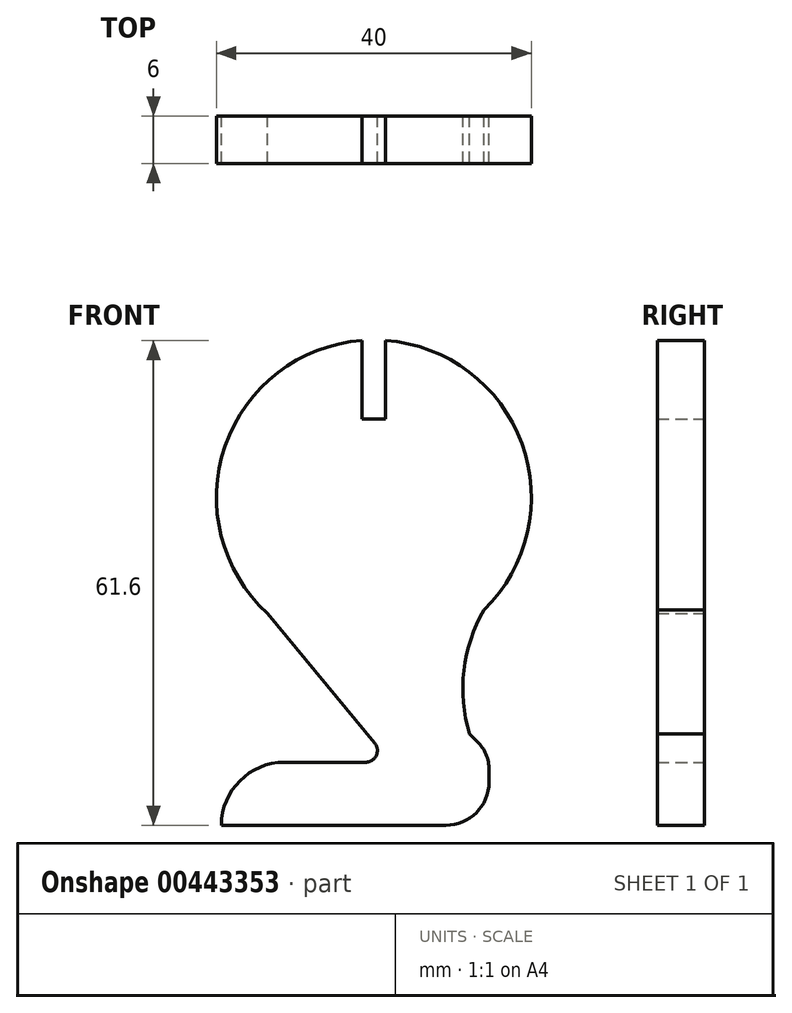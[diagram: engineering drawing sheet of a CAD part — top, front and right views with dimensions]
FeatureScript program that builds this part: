
annotation { "Feature Type Name" : "Feature", "Feature Type Description" : "" }
export const myFeature = defineFeature(function(context is Context, id is Id, definition is map)
    precondition{}
    {
        {
            var Q0;
            Q0=qCreatedBy(makeId("Front.planeOp"),FACE);
            var sketch = newSketch(context, id + "F0", { "sketchPlane" : qUnion([Q0])});
            skArc(sketch, "E0", {"start": v(-1.5, 36.94) * mm, "mid": v(-18.9, 23.55) * mm, "end": v(-13.52, 2.26) * mm});
            skLineSegment(sketch, "E1", {"start": v(-1.5, 36.94) * mm, "end": v(-1.5, 26.94) * mm});
            skLineSegment(sketch, "E2", {"start": v(-1.5, 26.94) * mm, "end": v(1.5, 26.94) * mm});
            skLineSegment(sketch, "E3", {"start": v(1.5, 26.94) * mm, "end": v(1.5, 36.94) * mm});
            skLineSegment(sketch, "E4", {"start": v(-13.52, 2.26) * mm, "end": v(0.1, -14.19) * mm});
            skPoint(sketch, "E5.orphan", {"position": v(-17, 6.46) * mm});
            skArc(sketch, "E6", {"start": v(14, 2.72) * mm, "mid": v(11.44, -4.97) * mm, "end": v(12.13, -13.04) * mm});
            skPoint(sketch, "E7.orphan", {"position": v(17.3, 6.96) * mm});
            skLineSegment(sketch, "E8", {"start": v(14.63, -17.58) * mm, "end": v(14.63, -19.16) * mm});
            skLineSegment(sketch, "E9", {"start": v(9.13, -24.66) * mm, "end": v(-18.34, -24.66) * mm});
            skPoint(sketch, "E10.visualSharp", {"position": v(14.63, -13.66) * mm});
            skArc(sketch, "E10.filletArc", {"start": v(14.63, -17.58) * mm, "mid": v(14.24, -15.63) * mm, "end": v(13.11, -14) * mm});
            skPoint(sketch, "E11.visualSharp", {"position": v(14.63, -24.66) * mm});
            skArc(sketch, "E11.filletArc", {"start": v(9.13, -24.66) * mm, "mid": v(13.02, -23.05) * mm, "end": v(14.63, -19.16) * mm});
            skPoint(sketch, "E12.endSnap0", {"position": v(14.62, -17.26) * mm});
            skLineSegment(sketch, "E13", {"start": v(-1.06, -16.64) * mm, "end": v(-11.37, -16.64) * mm});
            skPoint(sketch, "E14.visualSharp", {"position": v(-18.37, -16.64) * mm});
            skArc(sketch, "E14.filletArc", {"start": v(-11.37, -16.64) * mm, "mid": v(-17.02, -18.99) * mm, "end": v(-19.37, -24.64) * mm});
            skPoint(sketch, "E15.visualSharp", {"position": v(2.13, -16.64) * mm});
            skArc(sketch, "E15.filletArc", {"start": v(-1.06, -16.64) * mm, "mid": v(0.3, -15.78) * mm, "end": v(0.1, -14.19) * mm});
            skPoint(sketch, "E12.end.orphan", {"position": v(14.62, -13.64) * mm});
            skLineSegment(sketch, "E16", {"start": v(-18.4, -24.66) * mm, "end": v(-19.37, -24.64) * mm});
            skLineSegment(sketch, "E17", {"start": v(12.13, -13.04) * mm, "end": v(13.11, -14) * mm});
            skPoint(sketch, "E18.visualSharp", {"position": v(-18.37, -24.66) * mm});
            skArc(sketch, "E18.filletArc", {"start": v(-18.4, -24.66) * mm, "mid": v(-18.37, -24.66) * mm, "end": v(-18.34, -24.66) * mm});
            skArc(sketch, "E19.trimOffspring", {"start": v(14, 2.72) * mm, "mid": v(18.79, 23.86) * mm, "end": v(1.5, 36.94) * mm});
            skSolve(sketch);
        }
        {
            var Q0;
            Q0=makeQuery(id+"F0.imprint","IMPRINT",FACE,{"disambiguationData":[TD([[makeQuery(id+"F0.imprint","IMPRINT",EDGE,{"derivedFrom":sQuery(id+"F0.wireOp",EDGE,"E0")}),1.0]])]});
            extrude(context, id + "F1", {"entities" : qUnion([Q0]), "depth" : 3 * mm, "hasSecondDirection" : true, "secondDirectionOppositeDirection" : true, "secondDirectionDepth" : 3 * mm});
        }
    });
